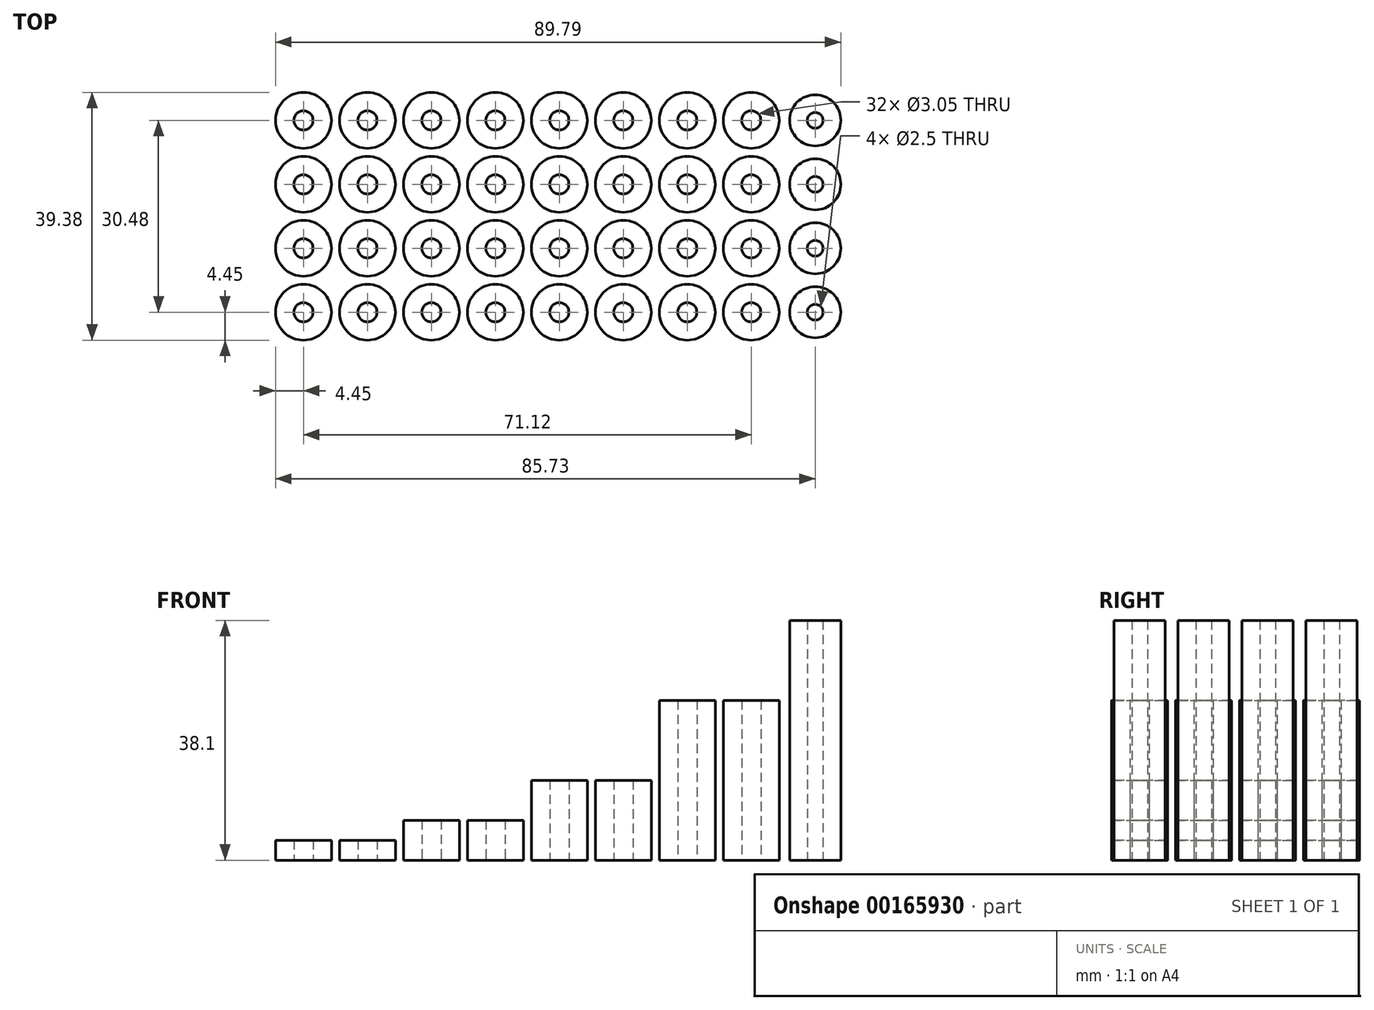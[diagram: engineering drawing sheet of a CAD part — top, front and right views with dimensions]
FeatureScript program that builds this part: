
annotation { "Feature Type Name" : "Feature", "Feature Type Description" : "" }
export const myFeature = defineFeature(function(context is Context, id is Id, definition is map)
    precondition{}
    {
        {
            var Q0;
            Q0=qCreatedBy(makeId("Top.planeOp"),FACE);
            var sketch = newSketch(context, id + "F0", { "sketchPlane" : qUnion([Q0])});
            skCircle(sketch, "E0", {"center": v(0, 0) * mm, "radius": 4.45 * mm});
            skCircle(sketch, "E1", {"center": v(0, 0) * mm, "radius": 1.52 * mm});
            skCircle(sketch, "E2.0.1.0", {"center": v(0, 10.16) * mm, "radius": 1.52 * mm});
            skCircle(sketch, "E2.0.1.1", {"center": v(0, 10.16) * mm, "radius": 4.45 * mm});
            skCircle(sketch, "E2.0.2.0", {"center": v(0, 20.32) * mm, "radius": 1.52 * mm});
            skCircle(sketch, "E2.0.2.1", {"center": v(0, 20.32) * mm, "radius": 4.45 * mm});
            skCircle(sketch, "E2.0.3.0", {"center": v(0, 30.48) * mm, "radius": 1.52 * mm});
            skCircle(sketch, "E2.0.3.1", {"center": v(0, 30.48) * mm, "radius": 4.45 * mm});
            skCircle(sketch, "E2.1.0.0", {"center": v(10.16, 0) * mm, "radius": 1.52 * mm});
            skCircle(sketch, "E2.1.0.1", {"center": v(10.16, 0) * mm, "radius": 4.45 * mm});
            skCircle(sketch, "E2.1.1.0", {"center": v(10.16, 10.16) * mm, "radius": 1.52 * mm});
            skCircle(sketch, "E2.1.1.1", {"center": v(10.16, 10.16) * mm, "radius": 4.45 * mm});
            skCircle(sketch, "E2.1.2.0", {"center": v(10.16, 20.32) * mm, "radius": 1.52 * mm});
            skCircle(sketch, "E2.1.2.1", {"center": v(10.16, 20.32) * mm, "radius": 4.45 * mm});
            skCircle(sketch, "E2.1.3.0", {"center": v(10.16, 30.48) * mm, "radius": 1.52 * mm});
            skCircle(sketch, "E2.1.3.1", {"center": v(10.16, 30.48) * mm, "radius": 4.45 * mm});
            skCircle(sketch, "E2.2.0.0", {"center": v(20.32, 0) * mm, "radius": 1.52 * mm});
            skCircle(sketch, "E2.2.0.1", {"center": v(20.32, 0) * mm, "radius": 4.45 * mm});
            skCircle(sketch, "E2.2.1.0", {"center": v(20.32, 10.16) * mm, "radius": 1.52 * mm});
            skCircle(sketch, "E2.2.1.1", {"center": v(20.32, 10.16) * mm, "radius": 4.45 * mm});
            skCircle(sketch, "E2.2.2.0", {"center": v(20.32, 20.32) * mm, "radius": 1.52 * mm});
            skCircle(sketch, "E2.2.2.1", {"center": v(20.32, 20.32) * mm, "radius": 4.45 * mm});
            skCircle(sketch, "E2.2.3.0", {"center": v(20.32, 30.48) * mm, "radius": 1.52 * mm});
            skCircle(sketch, "E2.2.3.1", {"center": v(20.32, 30.48) * mm, "radius": 4.45 * mm});
            skCircle(sketch, "E2.3.0.0", {"center": v(30.48, 0) * mm, "radius": 1.52 * mm});
            skCircle(sketch, "E2.3.0.1", {"center": v(30.48, 0) * mm, "radius": 4.45 * mm});
            skCircle(sketch, "E2.3.1.0", {"center": v(30.48, 10.16) * mm, "radius": 1.52 * mm});
            skCircle(sketch, "E2.3.1.1", {"center": v(30.48, 10.16) * mm, "radius": 4.45 * mm});
            skCircle(sketch, "E2.3.2.0", {"center": v(30.48, 20.32) * mm, "radius": 1.52 * mm});
            skCircle(sketch, "E2.3.2.1", {"center": v(30.48, 20.32) * mm, "radius": 4.45 * mm});
            skCircle(sketch, "E2.3.3.0", {"center": v(30.48, 30.48) * mm, "radius": 1.52 * mm});
            skCircle(sketch, "E2.3.3.1", {"center": v(30.48, 30.48) * mm, "radius": 4.45 * mm});
            skCircle(sketch, "E2.4.0.0", {"center": v(40.64, 0) * mm, "radius": 1.52 * mm});
            skCircle(sketch, "E2.4.0.1", {"center": v(40.64, 0) * mm, "radius": 4.45 * mm});
            skCircle(sketch, "E2.4.1.0", {"center": v(40.64, 10.16) * mm, "radius": 1.52 * mm});
            skCircle(sketch, "E2.4.1.1", {"center": v(40.64, 10.16) * mm, "radius": 4.45 * mm});
            skCircle(sketch, "E2.4.2.0", {"center": v(40.64, 20.32) * mm, "radius": 1.52 * mm});
            skCircle(sketch, "E2.4.2.1", {"center": v(40.64, 20.32) * mm, "radius": 4.45 * mm});
            skCircle(sketch, "E2.4.3.0", {"center": v(40.64, 30.48) * mm, "radius": 1.52 * mm});
            skCircle(sketch, "E2.4.3.1", {"center": v(40.64, 30.48) * mm, "radius": 4.45 * mm});
            skCircle(sketch, "E2.5.0.0", {"center": v(50.8, 0) * mm, "radius": 1.52 * mm});
            skCircle(sketch, "E2.5.0.1", {"center": v(50.8, 0) * mm, "radius": 4.45 * mm});
            skCircle(sketch, "E2.5.1.0", {"center": v(50.8, 10.16) * mm, "radius": 1.52 * mm});
            skCircle(sketch, "E2.5.1.1", {"center": v(50.8, 10.16) * mm, "radius": 4.45 * mm});
            skCircle(sketch, "E2.5.2.0", {"center": v(50.8, 20.32) * mm, "radius": 1.52 * mm});
            skCircle(sketch, "E2.5.2.1", {"center": v(50.8, 20.32) * mm, "radius": 4.45 * mm});
            skCircle(sketch, "E2.5.3.0", {"center": v(50.8, 30.48) * mm, "radius": 1.52 * mm});
            skCircle(sketch, "E2.5.3.1", {"center": v(50.8, 30.48) * mm, "radius": 4.45 * mm});
            skCircle(sketch, "E2.6.0.0", {"center": v(60.96, 0) * mm, "radius": 1.52 * mm});
            skCircle(sketch, "E2.6.0.1", {"center": v(60.96, 0) * mm, "radius": 4.45 * mm});
            skCircle(sketch, "E2.6.1.0", {"center": v(60.96, 10.16) * mm, "radius": 1.52 * mm});
            skCircle(sketch, "E2.6.1.1", {"center": v(60.96, 10.16) * mm, "radius": 4.45 * mm});
            skCircle(sketch, "E2.6.2.0", {"center": v(60.96, 20.32) * mm, "radius": 1.52 * mm});
            skCircle(sketch, "E2.6.2.1", {"center": v(60.96, 20.32) * mm, "radius": 4.45 * mm});
            skCircle(sketch, "E2.6.3.0", {"center": v(60.96, 30.48) * mm, "radius": 1.52 * mm});
            skCircle(sketch, "E2.6.3.1", {"center": v(60.96, 30.48) * mm, "radius": 4.45 * mm});
            skCircle(sketch, "E2.7.0.0", {"center": v(71.12, 0) * mm, "radius": 1.52 * mm});
            skCircle(sketch, "E2.7.0.1", {"center": v(71.12, 0) * mm, "radius": 4.45 * mm});
            skCircle(sketch, "E2.7.1.0", {"center": v(71.12, 10.16) * mm, "radius": 1.52 * mm});
            skCircle(sketch, "E2.7.1.1", {"center": v(71.12, 10.16) * mm, "radius": 4.45 * mm});
            skCircle(sketch, "E2.7.2.0", {"center": v(71.12, 20.32) * mm, "radius": 1.52 * mm});
            skCircle(sketch, "E2.7.2.1", {"center": v(71.12, 20.32) * mm, "radius": 4.45 * mm});
            skCircle(sketch, "E2.7.3.0", {"center": v(71.12, 30.48) * mm, "radius": 1.52 * mm});
            skCircle(sketch, "E2.7.3.1", {"center": v(71.12, 30.48) * mm, "radius": 4.45 * mm});
            skLineSegment(sketch, "E2.direction1", {"start": v(0, 0) * mm, "end": v(10.16, 0) * mm, "construction": true});
            skLineSegment(sketch, "E2.direction2", {"start": v(0, 0) * mm, "end": v(0, 10.16) * mm, "construction": true});
            skSolve(sketch);
        }
        {
            var Q0;
            Q0=makeQuery(id+"F0.imprint","IMPRINT",FACE,{"disambiguationData":[TD([[makeQuery(id+"F0.imprint","IMPRINT",EDGE,{"derivedFrom":sQuery(id+"F0.wireOp",EDGE,"E2.0.3.0")}),-1.0]])]});
            var Q1;
            Q1=makeQuery(id+"F0.imprint","IMPRINT",FACE,{"disambiguationData":[TD([[makeQuery(id+"F0.imprint","IMPRINT",EDGE,{"derivedFrom":sQuery(id+"F0.wireOp",EDGE,"E2.0.2.0")}),-1.0]])]});
            var Q2;
            Q2=makeQuery(id+"F0.imprint","IMPRINT",FACE,{"disambiguationData":[TD([[makeQuery(id+"F0.imprint","IMPRINT",EDGE,{"derivedFrom":sQuery(id+"F0.wireOp",EDGE,"E2.0.1.0")}),-1.0]])]});
            var Q3;
            Q3=makeQuery(id+"F0.imprint","IMPRINT",FACE,{"disambiguationData":[TD([[makeQuery(id+"F0.imprint","IMPRINT",EDGE,{"derivedFrom":sQuery(id+"F0.wireOp",EDGE,"E0")}),1.0]])]});
            var Q4;
            Q4=makeQuery(id+"F0.imprint","IMPRINT",FACE,{"disambiguationData":[TD([[makeQuery(id+"F0.imprint","IMPRINT",EDGE,{"derivedFrom":sQuery(id+"F0.wireOp",EDGE,"E2.1.0.0")}),-1.0]])]});
            var Q5;
            Q5=makeQuery(id+"F0.imprint","IMPRINT",FACE,{"disambiguationData":[TD([[makeQuery(id+"F0.imprint","IMPRINT",EDGE,{"derivedFrom":sQuery(id+"F0.wireOp",EDGE,"E2.1.1.0")}),-1.0]])]});
            var Q6;
            Q6=makeQuery(id+"F0.imprint","IMPRINT",FACE,{"disambiguationData":[TD([[makeQuery(id+"F0.imprint","IMPRINT",EDGE,{"derivedFrom":sQuery(id+"F0.wireOp",EDGE,"E2.1.2.0")}),-1.0]])]});
            var Q7;
            Q7=makeQuery(id+"F0.imprint","IMPRINT",FACE,{"disambiguationData":[TD([[makeQuery(id+"F0.imprint","IMPRINT",EDGE,{"derivedFrom":sQuery(id+"F0.wireOp",EDGE,"E2.1.3.0")}),-1.0]])]});
            extrude(context, id + "F1", {"entities" : qUnion([Q0, Q1, Q2, Q3, Q4, Q5, Q6, Q7]), "depth" : 3.17 * mm});
        }
        {
            var Q0;
            Q0=makeQuery(id+"F0.imprint","IMPRINT",FACE,{"disambiguationData":[TD([[makeQuery(id+"F0.imprint","IMPRINT",EDGE,{"derivedFrom":sQuery(id+"F0.wireOp",EDGE,"E2.2.3.0")}),-1.0]])]});
            var Q1;
            Q1=makeQuery(id+"F0.imprint","IMPRINT",FACE,{"disambiguationData":[TD([[makeQuery(id+"F0.imprint","IMPRINT",EDGE,{"derivedFrom":sQuery(id+"F0.wireOp",EDGE,"E2.2.2.0")}),-1.0]])]});
            var Q2;
            Q2=makeQuery(id+"F0.imprint","IMPRINT",FACE,{"disambiguationData":[TD([[makeQuery(id+"F0.imprint","IMPRINT",EDGE,{"derivedFrom":sQuery(id+"F0.wireOp",EDGE,"E2.2.1.0")}),-1.0]])]});
            var Q3;
            Q3=makeQuery(id+"F0.imprint","IMPRINT",FACE,{"disambiguationData":[TD([[makeQuery(id+"F0.imprint","IMPRINT",EDGE,{"derivedFrom":sQuery(id+"F0.wireOp",EDGE,"E2.2.0.0")}),-1.0]])]});
            var Q4;
            Q4=makeQuery(id+"F0.imprint","IMPRINT",FACE,{"disambiguationData":[TD([[makeQuery(id+"F0.imprint","IMPRINT",EDGE,{"derivedFrom":sQuery(id+"F0.wireOp",EDGE,"E2.3.0.0")}),-1.0]])]});
            var Q5;
            Q5=makeQuery(id+"F0.imprint","IMPRINT",FACE,{"disambiguationData":[TD([[makeQuery(id+"F0.imprint","IMPRINT",EDGE,{"derivedFrom":sQuery(id+"F0.wireOp",EDGE,"E2.3.1.0")}),-1.0]])]});
            var Q6;
            Q6=makeQuery(id+"F0.imprint","IMPRINT",FACE,{"disambiguationData":[TD([[makeQuery(id+"F0.imprint","IMPRINT",EDGE,{"derivedFrom":sQuery(id+"F0.wireOp",EDGE,"E2.3.2.0")}),-1.0]])]});
            var Q7;
            Q7=makeQuery(id+"F0.imprint","IMPRINT",FACE,{"disambiguationData":[TD([[makeQuery(id+"F0.imprint","IMPRINT",EDGE,{"derivedFrom":sQuery(id+"F0.wireOp",EDGE,"E2.3.3.0")}),-1.0]])]});
            extrude(context, id + "F2", {"entities" : qUnion([Q0, Q1, Q2, Q3, Q4, Q5, Q6, Q7]), "depth" : 6.35 * mm});
        }
        {
            var Q0;
            Q0=makeQuery(id+"F0.imprint","IMPRINT",FACE,{"disambiguationData":[TD([[makeQuery(id+"F0.imprint","IMPRINT",EDGE,{"derivedFrom":sQuery(id+"F0.wireOp",EDGE,"E2.4.3.0")}),-1.0]])]});
            var Q1;
            Q1=makeQuery(id+"F0.imprint","IMPRINT",FACE,{"disambiguationData":[TD([[makeQuery(id+"F0.imprint","IMPRINT",EDGE,{"derivedFrom":sQuery(id+"F0.wireOp",EDGE,"E2.4.2.0")}),-1.0]])]});
            var Q2;
            Q2=makeQuery(id+"F0.imprint","IMPRINT",FACE,{"disambiguationData":[TD([[makeQuery(id+"F0.imprint","IMPRINT",EDGE,{"derivedFrom":sQuery(id+"F0.wireOp",EDGE,"E2.4.1.0")}),-1.0]])]});
            var Q3;
            Q3=makeQuery(id+"F0.imprint","IMPRINT",FACE,{"disambiguationData":[TD([[makeQuery(id+"F0.imprint","IMPRINT",EDGE,{"derivedFrom":sQuery(id+"F0.wireOp",EDGE,"E2.4.0.0")}),-1.0]])]});
            var Q4;
            Q4=makeQuery(id+"F0.imprint","IMPRINT",FACE,{"disambiguationData":[TD([[makeQuery(id+"F0.imprint","IMPRINT",EDGE,{"derivedFrom":sQuery(id+"F0.wireOp",EDGE,"E2.5.0.0")}),-1.0]])]});
            var Q5;
            Q5=makeQuery(id+"F0.imprint","IMPRINT",FACE,{"disambiguationData":[TD([[makeQuery(id+"F0.imprint","IMPRINT",EDGE,{"derivedFrom":sQuery(id+"F0.wireOp",EDGE,"E2.5.1.0")}),-1.0]])]});
            var Q6;
            Q6=makeQuery(id+"F0.imprint","IMPRINT",FACE,{"disambiguationData":[TD([[makeQuery(id+"F0.imprint","IMPRINT",EDGE,{"derivedFrom":sQuery(id+"F0.wireOp",EDGE,"E2.5.2.0")}),-1.0]])]});
            var Q7;
            Q7=makeQuery(id+"F0.imprint","IMPRINT",FACE,{"disambiguationData":[TD([[makeQuery(id+"F0.imprint","IMPRINT",EDGE,{"derivedFrom":sQuery(id+"F0.wireOp",EDGE,"E2.5.3.0")}),-1.0]])]});
            extrude(context, id + "F3", {"entities" : qUnion([Q0, Q1, Q2, Q3, Q4, Q5, Q6, Q7]), "depth" : 12.7 * mm});
        }
        {
            var Q0;
            Q0=makeQuery(id+"F0.imprint","IMPRINT",FACE,{"disambiguationData":[TD([[makeQuery(id+"F0.imprint","IMPRINT",EDGE,{"derivedFrom":sQuery(id+"F0.wireOp",EDGE,"E2.6.3.0")}),-1.0]])]});
            var Q1;
            Q1=makeQuery(id+"F0.imprint","IMPRINT",FACE,{"disambiguationData":[TD([[makeQuery(id+"F0.imprint","IMPRINT",EDGE,{"derivedFrom":sQuery(id+"F0.wireOp",EDGE,"E2.6.2.0")}),-1.0]])]});
            var Q2;
            Q2=makeQuery(id+"F0.imprint","IMPRINT",FACE,{"disambiguationData":[TD([[makeQuery(id+"F0.imprint","IMPRINT",EDGE,{"derivedFrom":sQuery(id+"F0.wireOp",EDGE,"E2.6.1.0")}),-1.0]])]});
            var Q3;
            Q3=makeQuery(id+"F0.imprint","IMPRINT",FACE,{"disambiguationData":[TD([[makeQuery(id+"F0.imprint","IMPRINT",EDGE,{"derivedFrom":sQuery(id+"F0.wireOp",EDGE,"E2.6.0.0")}),-1.0]])]});
            var Q4;
            Q4=makeQuery(id+"F0.imprint","IMPRINT",FACE,{"disambiguationData":[TD([[makeQuery(id+"F0.imprint","IMPRINT",EDGE,{"derivedFrom":sQuery(id+"F0.wireOp",EDGE,"E2.7.3.0")}),-1.0]])]});
            var Q5;
            Q5=makeQuery(id+"F0.imprint","IMPRINT",FACE,{"disambiguationData":[TD([[makeQuery(id+"F0.imprint","IMPRINT",EDGE,{"derivedFrom":sQuery(id+"F0.wireOp",EDGE,"E2.7.2.0")}),-1.0]])]});
            var Q6;
            Q6=makeQuery(id+"F0.imprint","IMPRINT",FACE,{"disambiguationData":[TD([[makeQuery(id+"F0.imprint","IMPRINT",EDGE,{"derivedFrom":sQuery(id+"F0.wireOp",EDGE,"E2.7.1.0")}),-1.0]])]});
            var Q7;
            Q7=makeQuery(id+"F0.imprint","IMPRINT",FACE,{"disambiguationData":[TD([[makeQuery(id+"F0.imprint","IMPRINT",EDGE,{"derivedFrom":sQuery(id+"F0.wireOp",EDGE,"E2.7.0.0")}),-1.0]])]});
            extrude(context, id + "F4", {"entities" : qUnion([Q0, Q1, Q2, Q3, Q4, Q5, Q6, Q7]), "depth" : 25.4 * mm});
        }
        {
            var Q0;
            Q0=qCreatedBy(makeId("Top.planeOp"),FACE);
            var sketch = newSketch(context, id + "F5", { "sketchPlane" : qUnion([Q0])});
            skLineSegment(sketch, "E3", {"start": v(0, 0) * mm, "end": v(104.4, 0) * mm, "construction": true});
            skCircle(sketch, "E4", {"center": v(81.28, 0) * mm, "radius": 4.06 * mm});
            skCircle(sketch, "E5", {"center": v(81.28, 0) * mm, "radius": 1.25 * mm});
            skCircle(sketch, "E6.0.1.0", {"center": v(81.28, 10.16) * mm, "radius": 1.25 * mm});
            skCircle(sketch, "E6.0.1.1", {"center": v(81.28, 10.16) * mm, "radius": 4.06 * mm});
            skCircle(sketch, "E6.0.2.0", {"center": v(81.28, 20.32) * mm, "radius": 1.25 * mm});
            skCircle(sketch, "E6.0.2.1", {"center": v(81.28, 20.32) * mm, "radius": 4.06 * mm});
            skCircle(sketch, "E6.0.3.0", {"center": v(81.28, 30.48) * mm, "radius": 1.25 * mm});
            skCircle(sketch, "E6.0.3.1", {"center": v(81.28, 30.48) * mm, "radius": 4.06 * mm});
            skCircle(sketch, "E6.1.0.0", {"center": v(106.68, 0) * mm, "radius": 1.25 * mm});
            skCircle(sketch, "E6.1.0.1", {"center": v(106.68, 0) * mm, "radius": 4.06 * mm});
            skCircle(sketch, "E6.1.1.0", {"center": v(106.68, 10.16) * mm, "radius": 1.25 * mm});
            skCircle(sketch, "E6.1.1.1", {"center": v(106.68, 10.16) * mm, "radius": 4.06 * mm});
            skCircle(sketch, "E6.1.2.0", {"center": v(106.68, 20.32) * mm, "radius": 1.25 * mm});
            skCircle(sketch, "E6.1.2.1", {"center": v(106.68, 20.32) * mm, "radius": 4.06 * mm});
            skCircle(sketch, "E6.1.3.0", {"center": v(106.68, 30.48) * mm, "radius": 1.25 * mm});
            skCircle(sketch, "E6.1.3.1", {"center": v(106.68, 30.48) * mm, "radius": 4.06 * mm});
            skCircle(sketch, "E6.2.0.0", {"center": v(132.08, 0) * mm, "radius": 1.25 * mm});
            skCircle(sketch, "E6.2.0.1", {"center": v(132.08, 0) * mm, "radius": 4.06 * mm});
            skCircle(sketch, "E6.2.1.0", {"center": v(132.08, 10.16) * mm, "radius": 1.25 * mm});
            skCircle(sketch, "E6.2.1.1", {"center": v(132.08, 10.16) * mm, "radius": 4.06 * mm});
            skCircle(sketch, "E6.2.2.0", {"center": v(132.08, 20.32) * mm, "radius": 1.25 * mm});
            skCircle(sketch, "E6.2.2.1", {"center": v(132.08, 20.32) * mm, "radius": 4.06 * mm});
            skCircle(sketch, "E6.2.3.0", {"center": v(132.08, 30.48) * mm, "radius": 1.25 * mm});
            skCircle(sketch, "E6.2.3.1", {"center": v(132.08, 30.48) * mm, "radius": 4.06 * mm});
            skLineSegment(sketch, "E6.direction1", {"start": v(81.28, 0) * mm, "end": v(106.68, 0) * mm, "construction": true});
            skLineSegment(sketch, "E6.direction2", {"start": v(81.28, 0) * mm, "end": v(81.28, 10.16) * mm, "construction": true});
            skSolve(sketch);
        }
        {
            var Q0;
            Q0=makeQuery(id+"F5.imprint","IMPRINT",FACE,{"disambiguationData":[TD([[makeQuery(id+"F5.imprint","IMPRINT",EDGE,{"derivedFrom":sQuery(id+"F5.wireOp",EDGE,"E4")}),1.0]])]});
            var Q1;
            Q1=makeQuery(id+"F5.imprint","IMPRINT",FACE,{"disambiguationData":[TD([[makeQuery(id+"F5.imprint","IMPRINT",EDGE,{"derivedFrom":sQuery(id+"F5.wireOp",EDGE,"E6.0.1.0")}),-1.0]])]});
            var Q2;
            Q2=makeQuery(id+"F5.imprint","IMPRINT",FACE,{"disambiguationData":[TD([[makeQuery(id+"F5.imprint","IMPRINT",EDGE,{"derivedFrom":sQuery(id+"F5.wireOp",EDGE,"E6.0.2.0")}),-1.0]])]});
            var Q3;
            Q3=makeQuery(id+"F5.imprint","IMPRINT",FACE,{"disambiguationData":[TD([[makeQuery(id+"F5.imprint","IMPRINT",EDGE,{"derivedFrom":sQuery(id+"F5.wireOp",EDGE,"E6.0.3.0")}),-1.0]])]});
            extrude(context, id + "F6", {"entities" : qUnion([Q0, Q1, Q2, Q3]), "depth" : 38.1 * mm});
        }
    });
